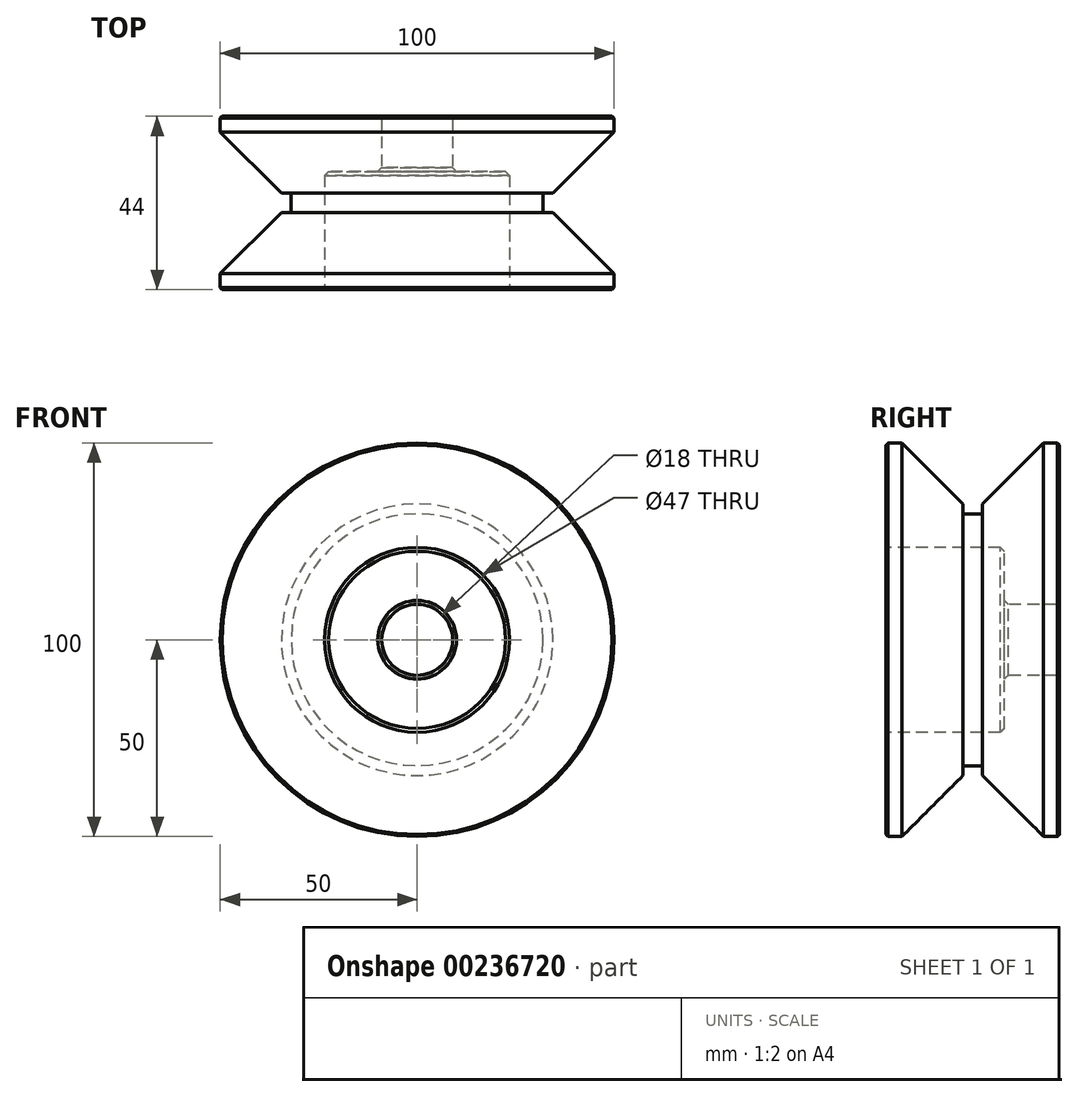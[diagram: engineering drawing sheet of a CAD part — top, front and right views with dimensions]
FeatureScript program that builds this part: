
annotation { "Feature Type Name" : "Feature", "Feature Type Description" : "" }
export const myFeature = defineFeature(function(context is Context, id is Id, definition is map)
    precondition{}
    {
        {
            var Q0;
            Q0=qCreatedBy(makeId("Right.planeOp"),FACE);
            var sketch = newSketch(context, id + "F0", { "sketchPlane" : qUnion([Q0])});
            skLineSegment(sketch, "E0", {"start": v(3.5, 9) * mm, "end": v(3.5, 50) * mm});
            skLineSegment(sketch, "E1", {"start": v(3.5, 50) * mm, "end": v(-0.5, 50) * mm});
            skLineSegment(sketch, "E2", {"start": v(-0.5, 50) * mm, "end": v(-16, 34.5) * mm});
            skLineSegment(sketch, "E3", {"start": v(-21, 34.5) * mm, "end": v(-36.5, 50) * mm});
            skLineSegment(sketch, "E4", {"start": v(-36.5, 50) * mm, "end": v(-40.5, 50) * mm});
            skLineSegment(sketch, "E5", {"start": v(-40.5, 50) * mm, "end": v(-40.5, 9) * mm});
            skLineSegment(sketch, "E6", {"start": v(-40.5, 0) * mm, "end": v(-0.2, 0) * mm, "construction": true});
            skLineSegment(sketch, "E7", {"start": v(3.5, 9) * mm, "end": v(-40.5, 9) * mm});
            skLineSegment(sketch, "E8", {"start": v(-16, 34.5) * mm, "end": v(-16, 32) * mm});
            skLineSegment(sketch, "E9", {"start": v(-16, 32) * mm, "end": v(-21, 32) * mm});
            skLineSegment(sketch, "E10", {"start": v(-21, 32) * mm, "end": v(-21, 34.5) * mm});
            skPoint(sketch, "E11.orphan", {"position": v(-18.5, 32) * mm});
            skSolve(sketch);
        }
        {
            var Q0;
            Q0=qSketchRegion(id+"F0",true);
            var Q1;
            Q1=makeQuery(id+"F0.imprint","IMPRINT",FACE,{"disambiguationData":[TD([[makeQuery(id+"F0.imprint","IMPRINT",EDGE,{"derivedFrom":sQuery(id+"F0.wireOp",EDGE,"E0")}),1.0]])]});
            var Q2;
            Q2=sQuery(id+"F0.wireOp",EDGE,"E6");
            revolve(context, id + "F1", {"entities" : qUnion([Q0, Q1]), "axis" : qUnion([Q2]), "revolveType" : RevolveType.FULL});
        }
        {
            var Q0;
            Q0=makeQuery(id+"F1.opRevolve","SWEPT_EDGE",EDGE,{"disambiguationData":[OSD([sQuery(id+"F0.wireOp",EDGE,"E5"),sQuery(id+"F0.wireOp",EDGE,"E7")])]});
            var Q1;
            Q1=makeQuery(id+"F1.opRevolve","SWEPT_EDGE",EDGE,{"disambiguationData":[OSD([sQuery(id+"F0.wireOp",EDGE,"E4"),sQuery(id+"F0.wireOp",EDGE,"E5")])]});
            var Q2;
            Q2=makeQuery(id+"F1.opRevolve","SWEPT_EDGE",EDGE,{"disambiguationData":[OSD([sQuery(id+"F0.wireOp",EDGE,"E0"),sQuery(id+"F0.wireOp",EDGE,"E1")])]});
            var Q3;
            Q3=makeQuery(id+"F1.opRevolve","SWEPT_EDGE",EDGE,{"disambiguationData":[OSD([sQuery(id+"F0.wireOp",EDGE,"E0"),sQuery(id+"F0.wireOp",EDGE,"E7")])]});
            chamfer(context, id + "F2", {"entities" : qUnion([Q0, Q1, Q2, Q3]), "width" : 0.5 * mm, "tangentPropagation" : true});
        }
        {
            var Q0;
            Q0=makeQuery(id+"F1.opRevolve","SWEPT_FACE",FACE,{"disambiguationData":[OSD([sQuery(id+"F0.wireOp",EDGE,"E5")])]});
            var sketch = newSketch(context, id + "F3", { "sketchPlane" : qUnion([Q0])});
            skCircle(sketch, "E12", {"center": v(0, 0) * mm, "radius": 23.5 * mm});
            skSolve(sketch);
        }
        {
            var Q0;
            Q0=qSketchRegion(id+"F3",true);
            extrude(context, id + "F4", {"entities" : qUnion([Q0]), "operationType" : NewBodyOperationType.REMOVE, "oppositeDirection" : true, "depth" : 30 * mm, "offsetDistance" : 25 * mm});
        }
        {
            var Q0;
            Q0=makeQuery(id+"FnWQ70JvMq0tRNy_1.boolean.opBoolean","COPY",EDGE,{"derivedFrom":makeQuery(id+"FnWQ70JvMq0tRNy_1.opExtrude","CAP_EDGE",EDGE,{"disambiguationData":[OSD([sQuery(id+"FXHlYBymdNhZE7z_1.wireOp",EDGE,"a6LdQnEW-Pwt0-sgRs-2Upj-iUyv4hqqTHH1")])],"isStart":true})});
            var Q1;
            Q1=makeQuery(id+"F4.boolean.opBoolean","COPY",EDGE,{"derivedFrom":makeQuery(id+"F4.opExtrude","CAP_EDGE",EDGE,{"disambiguationData":[OSD([sQuery(id+"F3.wireOp",EDGE,"E12")])],"isStart":true})});
            var Q2;
            Q2=makeQuery(id+"F4.boolean.opBoolean","INTERSECT",EDGE,{"derivedFrom":[makeQuery(id+"F1.opRevolve","SWEPT_FACE",FACE,{"disambiguationData":[OSD([sQuery(id+"F0.wireOp",EDGE,"E7")])]}),makeQuery(id+"F4.opExtrude","CAP_FACE",FACE,{"disambiguationData":[OSD([sQuery(id+"F3.wireOp",EDGE,"E12")])],"isStart":false})]});
            var Q3;
            Q3=makeQuery(id+"F4.boolean.opBoolean","COPY",EDGE,{"derivedFrom":makeQuery(id+"F4.opExtrude","CAP_EDGE",EDGE,{"disambiguationData":[OSD([sQuery(id+"F3.wireOp",EDGE,"E12")])],"isStart":false})});
            var Q4;
            Q4=makeQuery(id+"FnWQ70JvMq0tRNy_1.boolean.opBoolean","COPY",EDGE,{"derivedFrom":makeQuery(id+"FnWQ70JvMq0tRNy_1.opExtrude","CAP_EDGE",EDGE,{"disambiguationData":[OSD([sQuery(id+"FXHlYBymdNhZE7z_1.wireOp",EDGE,"a6LdQnEW-Pwt0-sgRs-2Upj-iUyv4hqqTHH1")])],"isStart":false})});
            var Q5;
            Q5=makeQuery(id+"FnWQ70JvMq0tRNy_1.boolean.opBoolean","INTERSECT",EDGE,{"derivedFrom":[makeQuery(id+"F1.opRevolve","SWEPT_FACE",FACE,{"disambiguationData":[OSD([sQuery(id+"F0.wireOp",EDGE,"E7")])]}),makeQuery(id+"FnWQ70JvMq0tRNy_1.opExtrude","CAP_FACE",FACE,{"disambiguationData":[OSD([sQuery(id+"FXHlYBymdNhZE7z_1.wireOp",EDGE,"a6LdQnEW-Pwt0-sgRs-2Upj-iUyv4hqqTHH1")])],"isStart":false})]});
            chamfer(context, id + "F5", {"entities" : qUnion([Q0, Q1, Q2, Q3, Q4, Q5]), "width" : 1 * mm, "tangentPropagation" : true});
        }
    });
